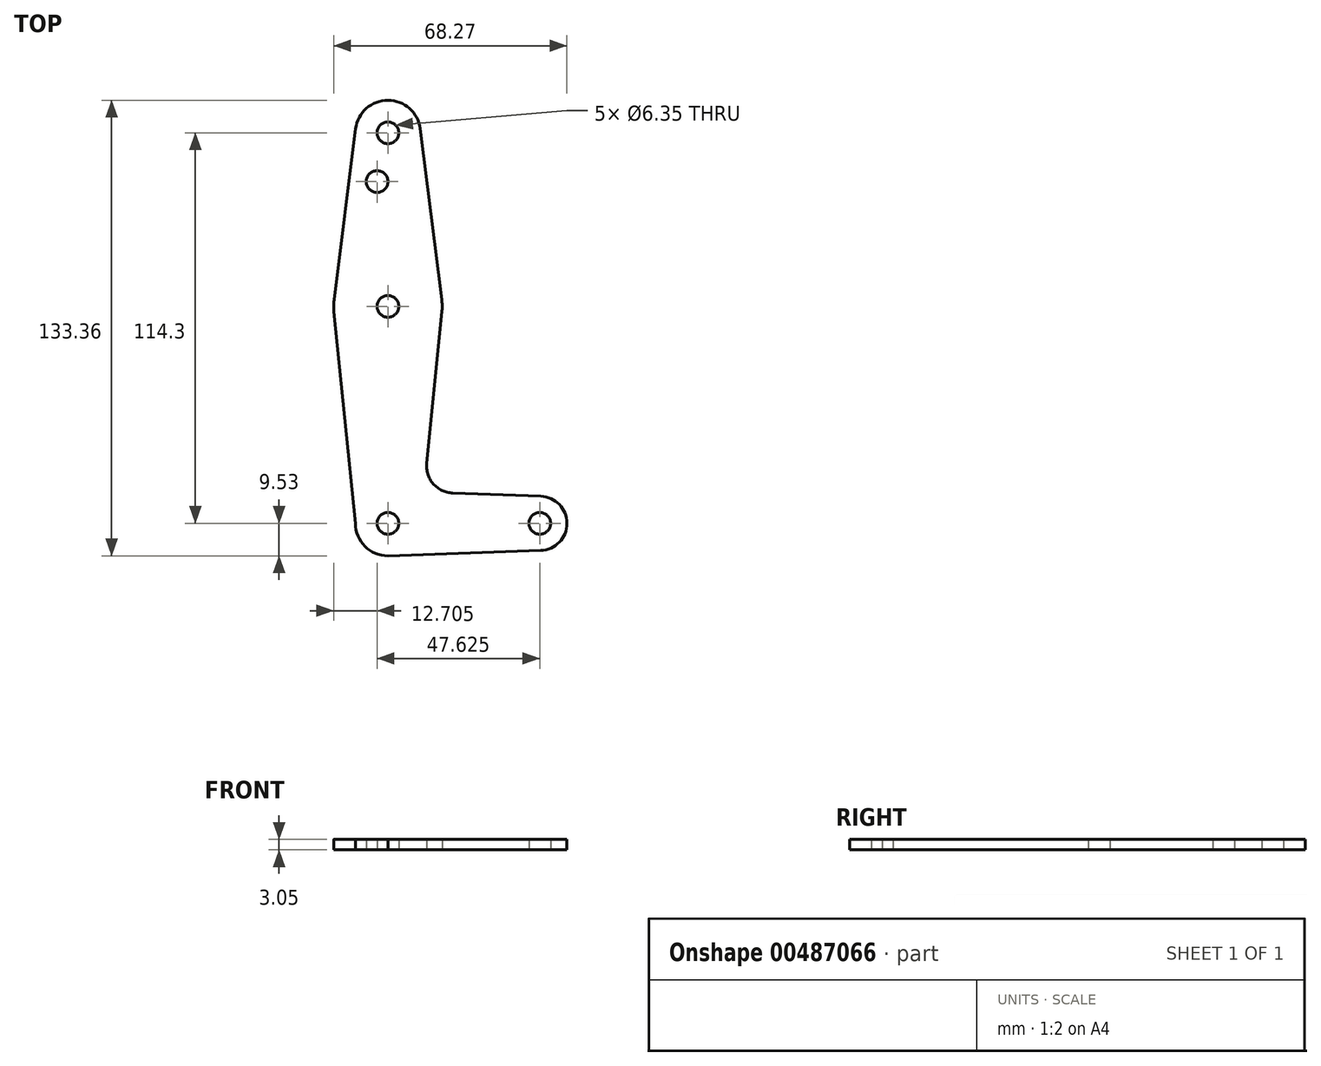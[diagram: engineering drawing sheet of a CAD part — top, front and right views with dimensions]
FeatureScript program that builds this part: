
annotation { "Feature Type Name" : "Feature", "Feature Type Description" : "" }
export const myFeature = defineFeature(function(context is Context, id is Id, definition is map)
    precondition{}
    {
        {
            var Q0;
            Q0=qCreatedBy(makeId("Top.planeOp"),FACE);
            var sketch = newSketch(context, id + "F0", { "sketchPlane" : qUnion([Q0])});
            skLineSegment(sketch, "E0", {"start": v(0, 0) * mm, "end": v(0, 114.3) * mm, "construction": true});
            skLineSegment(sketch, "E1", {"start": v(0, 0) * mm, "end": v(44.45, 0) * mm, "construction": true});
            skCircle(sketch, "E2", {"center": v(0, 0) * mm, "radius": 9.53 * mm});
            skCircle(sketch, "E3", {"center": v(0, 114.3) * mm, "radius": 9.53 * mm});
            skCircle(sketch, "E4", {"center": v(44.45, 0) * mm, "radius": 7.94 * mm});
            skCircle(sketch, "E5", {"center": v(0, 63.5) * mm, "radius": 15.88 * mm});
            skCircle(sketch, "E6", {"center": v(0, 114.3) * mm, "radius": 3.18 * mm});
            skCircle(sketch, "E7", {"center": v(0, 63.5) * mm, "radius": 3.18 * mm});
            skCircle(sketch, "E8", {"center": v(0, 0) * mm, "radius": 3.18 * mm});
            skCircle(sketch, "E9", {"center": v(44.45, 0) * mm, "radius": 3.18 * mm});
            skLineSegment(sketch, "E10", {"start": v(9.45, 115.5) * mm, "end": v(15.75, 65.48) * mm});
            skLineSegment(sketch, "E11", {"start": v(-9.45, 115.5) * mm, "end": v(-15.75, 65.48) * mm});
            skLineSegment(sketch, "E12", {"start": v(15.8, 61.91) * mm, "end": v(11.34, 17.6) * mm});
            skLineSegment(sketch, "E13", {"start": v(44.73, 7.93) * mm, "end": v(18.97, 8.85) * mm});
            skLineSegment(sketch, "E14", {"start": v(-9.53, 0) * mm, "end": v(-15.8, 61.9) * mm});
            skLineSegment(sketch, "E15", {"start": v(0, -9.53) * mm, "end": v(44.73, -7.93) * mm});
            skPoint(sketch, "E16.newPointB", {"position": v(0, 9.53) * mm});
            skArc(sketch, "E16.filletArc", {"start": v(11.34, 17.6) * mm, "mid": v(13.26, 11.57) * mm, "end": v(18.97, 8.85) * mm});
            skCircle(sketch, "E17", {"center": v(-3.18, 100.03) * mm, "radius": 3.18 * mm});
            skSolve(sketch);
        }
        {
            var Q0;
            Q0=makeQuery(id+"F0.imprint","IMPRINT",FACE,{"disambiguationData":[TD([[makeQuery(id+"F0.imprint","IMPRINT",EDGE,{"derivedFrom":sQuery(id+"F0.wireOp",EDGE,"E9")}),-1.0]])]});
            var Q1;
            Q1=makeQuery(id+"F0.imprint","IMPRINT",FACE,{"disambiguationData":[TD([[makeQuery(id+"F0.imprint","IMPRINT",EDGE,{"derivedFrom":sQuery(id+"F0.wireOp",EDGE,"E8")}),-1.0]])]});
            var Q2;
            {var subQ0=sQuery(id+"F0.wireOp",EDGE,"E12");Q2=makeQuery(id+"F0.imprint","IMPRINT",FACE,{"disambiguationData":[TD([[makeQuery(id+"F0.imprint","IMPRINT",EDGE,{"derivedFrom":subQ0}),-1.0]])]});}
            var Q3;
            {var subQ1=sQuery(id+"F0.wireOp",EDGE,"E10");Q3=makeQuery(id+"F0.imprint","IMPRINT",FACE,{"disambiguationData":[TD([[makeQuery(id+"F0.imprint","IMPRINT",EDGE,{"derivedFrom":subQ1}),-1.0]])]});}
            var Q4;
            Q4=makeQuery(id+"F0.imprint","IMPRINT",FACE,{"disambiguationData":[TD([[makeQuery(id+"F0.imprint","IMPRINT",EDGE,{"derivedFrom":sQuery(id+"F0.wireOp",EDGE,"E7")}),-1.0]])]});
            var Q5;
            {var subQ0=sQuery(id+"F0.wireOp",EDGE,"E15");var subQ1=sQuery(id+"F0.wireOp",EDGE,"E2");var subQ2=makeQuery(id+"F0.imprint","INTERSECT",VERTEX,{"disambiguationData":[OD(0.0)],"derivedFrom":[subQ1,subQ0]});Q5=makeQuery(id+"F0.imprint","IMPRINT",FACE,{"disambiguationData":[TD([[makeQuery(id+"F0.imprint","IMPRINT",EDGE,{"disambiguationData":[TD([[subQ2,-1.0]])],"derivedFrom":subQ1}),1.0]])]});}
            var Q6;
            Q6=makeQuery(id+"F0.imprint","IMPRINT",FACE,{"disambiguationData":[TD([[makeQuery(id+"F0.imprint","IMPRINT",EDGE,{"derivedFrom":sQuery(id+"F0.wireOp",EDGE,"E6")}),-1.0]])]});
            extrude(context, id + "F1", {"entities" : qUnion([Q0, Q1, Q2, Q3, Q4, Q5, Q6]), "depth" : 3.05 * mm});
        }
    });
